# Revit family: LEGRAND_NON INTERLOCKED SOCKETS_FLUSH MOUNTED_IP66_230
name_source: partatom
category: Installations électriques
revit_build: Autodesk Revit 2018 (Build: 20170223_1515(x64)
units: mm (PartAtom-declared; Revit-internal decimal feet)

## family parameters
Conserver l'orientation des annotations = Non
Cote de connecteur circulaire = Utiliser le diamètre
Couper avec des vides une fois chargée = Non
Hôte = Face
Partagée = Non
Point de calcul de pièce = Non
Type d'élément = Normal

## types (9) — shared parameters
Description = international standard socket for flush or surface mounting with accessory allows the connection of power devices
Elévation par défaut = 1000 mm  [stored 3.28084 ft]
Fabricant = Legrand
Flush E or Surface mounting S = flush and surface mounting
General Conditions of Use = https://export.legrand.com
Maximum installation temperature = 40°C
Maximum use temperature = 100°C
Minimum installation temperature = -20°C
Minimum use temperature = -50°C
Tension V = 230 V  50/60 Hz blue
characteristic color = blue
connecting type = screw terminals
halogen free = Non
material of box = plastic
protection class IP = IP66/67-55
resistance to chocks IK = 09

## per-type parameters (varying)
| type | Dia bouchon | Modèle | Number of poles | Position of earth h | RAY BOUCHON | Ray | Standard IEC or NFC | dIA | depth for flush mounting mm | depth mm | h1 | height mm | horizontal fixing distance mm | intensity A | vertical fixing distance mm | width mm |
| panel mounting socket Hypra   IP66/67-55   16 A   200/250 V   2P+E   plast | 68 mm | 051126 | 3 | 6 | 34 mm | 21 mm  [stored 0.0688976 ft] | IEC | 42 mm | 40 mm | 85 mm | 43 mm | 72 mm | 52 mm | 16 A | 60 mm | 64 mm |
| panel mounting socket Hypra   IP66/67-55   16 A   200/250 V   3P+E   plast | 79 mm | 051127 | 6 | 6 | 40 mm | 24 mm | IEC | 49 mm | 41 mm | 89 mm  [stored 0.291995 ft] | 50 mm | 84 mm | 60 mm | 16 A | 70 mm | 74 mm |
| panel mounting socket single fixing center Hypra  IP66/67-55  16 A   200/250 V   2P+E   plast | 84 mm | 051146 | 3 | 6 | 42 mm | 26 mm | IEC | 52 mm | 42 mm | 81 mm | 50 mm | 84 mm | 70 mm | 16 A | 70 mm | 84 mm |
| panel mounting socket single fixing center Hypra  IP66/67-55  16 A   200/250 V   3P+E   plast | 84 mm | 051147 | 4 | 9 | 42 mm | 26 mm | IEC | 52 mm | 43 mm | 84 mm | 50 mm | 84 mm | 70 mm | 16 A | 70 mm | 84 mm |
| panel mounting socket single fixing center Hypra  IP66/67-55  32 A   200/250 V   2P+E   plast | 89 mm  [stored 0.291995 ft] | 053046 | 3 | 6 | 45 mm | 27 mm | IEC | 55 mm | 54 mm | 104 mm | 56 mm | 94 mm | 70 mm | 32 A | 70 mm | 84 mm |
| panel mounting socket single fixing center Hypra  IP66/67-55  32 A   230 V   3P+E   plast | 89 mm  [stored 0.291995 ft] | 053047 | 4 | 9 | 45 mm | 27 mm | IEC | 55 mm | 54 mm | 104 mm | 56 mm | 94 mm | 70 mm | 32 A | 70 mm | 84 mm |
| panel mounting socket Hypra   IP66/67-55  16 A   250 V   2P+E   domestic standard   plast | 67 mm | 053911 | 3 | 6 | 34 mm | 21 mm  [stored 0.0688976 ft] | NFC | 41 mm | 15 mm | 63 mm  [stored 0.206693 ft] | 40 mm | 67 mm | 55 mm | 16 A | 55 mm | 67 mm |
| panel mounting socket Hypra  IP66/67-55   63A   200 250 V   2P+E   plast | 106 mm | 059326 | 3 | 6 | 53 mm | 33 mm | IEC | 65 mm | 85 mm | 164 mm | 64 mm | 106 mm | 77 mm | 63 A | 85 mm | 106 mm |
| panel mounting socket Hypra  IP66/67-55  63 A    230 V   3P+E  plast | 106 mm | 059327 | 4 | 9 | 53 mm | 33 mm | IEC | 65 mm | 85 mm | 164 mm | 64 mm | 106 mm | 77 mm | 63 A | 85 mm | 106 mm |

note: [stored X ft] marks values corroborated as IEEE doubles in the binary element streams (Revit-internal decimal feet)
